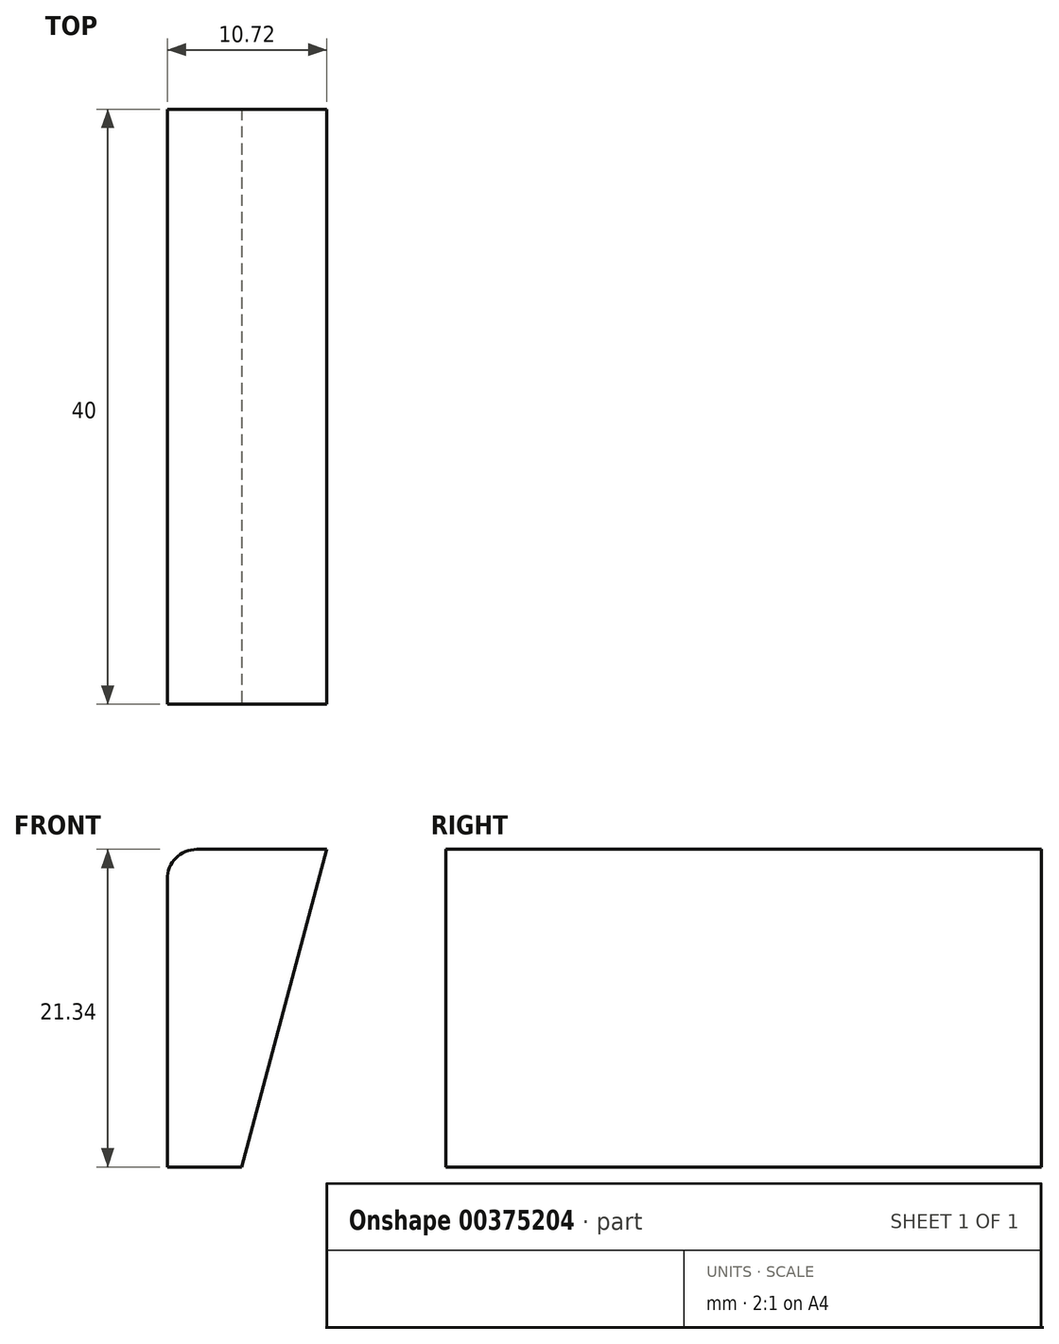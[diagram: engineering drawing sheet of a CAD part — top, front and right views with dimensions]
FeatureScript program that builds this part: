
annotation { "Feature Type Name" : "Feature", "Feature Type Description" : "" }
export const myFeature = defineFeature(function(context is Context, id is Id, definition is map)
    precondition{}
    {
        {
            var Q0;
            Q0=qCreatedBy(makeId("Front.planeOp"),FACE);
            var sketch = newSketch(context, id + "F0", { "sketchPlane" : qUnion([Q0])});
            skLineSegment(sketch, "E0", {"start": v(0, 0) * mm, "end": v(10.72, 0) * mm});
            skLineSegment(sketch, "E1", {"start": v(10.72, 0) * mm, "end": v(0, -40) * mm});
            skLineSegment(sketch, "E2", {"start": v(0, -40) * mm, "end": v(0, 0) * mm});
            skSolve(sketch);
        }
        {
            var Q0;
            Q0 = qSketchRegion(id + "F0", true);
            extrude(context, id + "F1", {"entities" : qUnion([Q0]), "depth" : 40 * mm});
        }
        {
            var Q0;
            Q0=makeQuery(id+"F1.opExtrude","CAP_FACE",FACE,{"disambiguationData":[OSD([sQuery(id+"F0.wireOp",EDGE,"E0"),sQuery(id+"F0.wireOp",EDGE,"E1"),sQuery(id+"F0.wireOp",EDGE,"E2")])],"isStart":false});
            var sketch = newSketch(context, id + "F2", { "sketchPlane" : qUnion([Q0])});
            skLineSegment(sketch, "E3", {"start": v(0, -21.34) * mm, "end": v(5, -21.34) * mm});
            skLineSegment(sketch, "E4", {"start": v(5, -21.34) * mm, "end": v(5, -40) * mm});
            skLineSegment(sketch, "E5", {"start": v(5, -40) * mm, "end": v(0, -40) * mm});
            skLineSegment(sketch, "E6", {"start": v(0, -40) * mm, "end": v(0, -21.34) * mm});
            skSolve(sketch);
        }
        {
            var Q0;
            Q0 = qSketchRegion(id + "F2", true);
            extrude(context, id + "F3", {"entities" : qUnion([Q0]), "operationType" : NewBodyOperationType.REMOVE, "endBound" : BoundingType.THROUGH_ALL, "oppositeDirection" : true, "depth" : 25.4 * mm});
        }
        {
            var Q0;
            Q0=makeQuery(id+"F1.opExtrude","SWEPT_EDGE",EDGE,{"disambiguationData":[OSD([sQuery(id+"F0.wireOp",EDGE,"E0"),sQuery(id+"F0.wireOp",EDGE,"E2")])]});
            var Q1;
            Q1=makeQuery(id+"F3.boolean.opBoolean","COPY",EDGE,{"derivedFrom":makeQuery(id+"F3.opExtrude","SWEPT_EDGE",EDGE,{"disambiguationData":[OSD([sQuery(id+"F0.wireOp",EDGE,"E2"),sQuery(id+"F2.wireOp",EDGE,"E3"),sQuery(id+"F2.wireOp",EDGE,"E6")])]})});
            fillet(context, id + "F4", {"entities" : qUnion([Q0, Q1]), "radius" : 2 * mm, "tangentPropagation" : true, "allowEdgeOverflow" : false});
        }
    });
